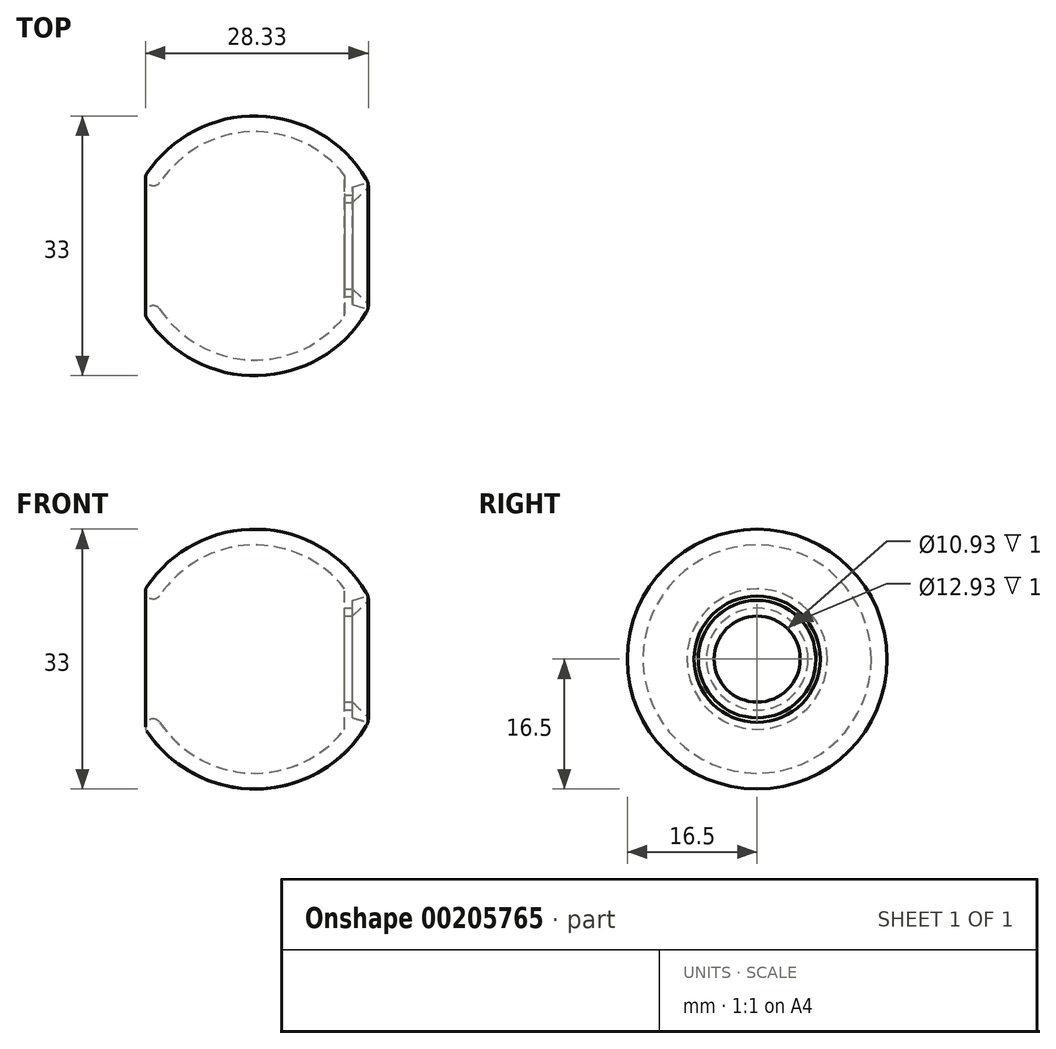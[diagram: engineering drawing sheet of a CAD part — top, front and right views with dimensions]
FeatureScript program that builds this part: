
annotation { "Feature Type Name" : "Feature", "Feature Type Description" : "" }
export const myFeature = defineFeature(function(context is Context, id is Id, definition is map)
    precondition{}
    {
        {
            var Q0;
            Q0=qCreatedBy(makeId("Front.planeOp"),FACE);
            var sketch = newSketch(context, id + "F0", { "sketchPlane" : qUnion([Q0])});
            skArc(sketch, "E0", {"start": v(15.56, 8) * mm, "mid": v(-17.5, 0) * mm, "end": v(15.56, -8) * mm});
            skArc(sketch, "E1", {"start": v(15.56, -8) * mm, "mid": v(19, 0) * mm, "end": v(15.56, 8) * mm});
            skPoint(sketch, "E2", {"position": v(15.56, 8) * mm});
            skPoint(sketch, "E3", {"position": v(15.56, -8) * mm});
            skPoint(sketch, "E4", {"position": v(19, 0) * mm});
            skPoint(sketch, "E5", {"position": v(17.5, 0) * mm});
            skArc(sketch, "E6", {"start": v(15.56, -8) * mm, "mid": v(17.5, 0) * mm, "end": v(15.56, 8) * mm, "construction": true});
            skLineSegment(sketch, "E7", {"start": v(15.56, 8) * mm, "end": v(15.56, -8) * mm, "construction": true});
            skPoint(sketch, "E8", {"position": v(15.56, 0) * mm});
            skSolve(sketch);
        }
        {
            var Q0;
            Q0=qCreatedBy(makeId("Front.planeOp"),FACE);
            var sketch = newSketch(context, id + "F1", { "sketchPlane" : qUnion([Q0])});
            skArc(sketch, "E9.0", {"start": v(14.15, 8.5) * mm, "mid": v(0.4, 16.5) * mm, "end": v(-13.73, 9.15) * mm});
            skLineSegment(sketch, "E10", {"start": v(14.43, 7.46) * mm, "end": v(14.43, 0) * mm, "construction": true});
            skLineSegment(sketch, "E11", {"start": v(14.43, 0) * mm, "end": v(-16.5, 0) * mm, "construction": true});
            skArc(sketch, "E12.0", {"start": v(11.43, 8.92) * mm, "mid": v(-0.54, 14.49) * mm, "end": v(-12.06, 8.05) * mm});
            skPoint(sketch, "E13.orphan", {"position": v(14.43, -8) * mm});
            skLineSegment(sketch, "E14", {"start": v(0, 0) * mm, "end": v(-15.16, 8.75) * mm, "construction": true});
            skLineSegment(sketch, "E15", {"start": v(0, 0) * mm, "end": v(11.25, 13.4) * mm, "construction": true});
            skArc(sketch, "E16", {"start": v(-13.73, 9.15) * mm, "mid": v(-13.45, 7.77) * mm, "end": v(-12.06, 8.05) * mm});
            skPoint(sketch, "E17.visualSharp", {"position": v(14.43, 8) * mm});
            skArc(sketch, "E17.filletArc", {"start": v(14.35, 8.02) * mm, "mid": v(14.27, 8.26) * mm, "end": v(14.15, 8.5) * mm});
            skArc(sketch, "E18", {"start": v(14.43, 7.46) * mm, "mid": v(14.41, 7.74) * mm, "end": v(14.35, 8.02) * mm, "construction": true});
            skLineSegment(sketch, "E19", {"start": v(11.43, 8.92) * mm, "end": v(11.43, 6.46) * mm});
            skLineSegment(sketch, "E20", {"start": v(14.35, 8.02) * mm, "end": v(12.43, 7.46) * mm});
            skLineSegment(sketch, "E21", {"start": v(12.43, 7.46) * mm, "end": v(12.43, 6.46) * mm});
            skLineSegment(sketch, "E22", {"start": v(12.43, 6.46) * mm, "end": v(11.43, 6.46) * mm});
            skSolve(sketch);
        }
        {
            var Q0;
            Q0 = qSketchRegion(id + "F1", true);
            var Q1;
            Q1=sQuery(id+"F1.wireOp",EDGE,"E11");
            revolve(context, id + "F2", {"entities" : qUnion([Q0]), "axis" : qUnion([Q1]), "revolveType" : RevolveType.FULL});
        }
        {
            var Q0;
            Q0=qCreatedBy(makeId("Front.planeOp"),FACE);
            var sketch = newSketch(context, id + "F3", { "sketchPlane" : qUnion([Q0])});
            skArc(sketch, "E23.0", {"start": v(14.43, 7.46) * mm, "mid": v(14.41, 7.74) * mm, "end": v(14.35, 8.02) * mm});
            skLineSegment(sketch, "E23.1", {"start": v(14.35, 8.02) * mm, "end": v(12.43, 7.46) * mm});
            skLineSegment(sketch, "E23.2", {"start": v(12.43, 7.46) * mm, "end": v(12.43, 6.46) * mm});
            skLineSegment(sketch, "E23.3", {"start": v(12.43, 6.46) * mm, "end": v(11.43, 6.46) * mm});
            skLineSegment(sketch, "E24", {"start": v(11.43, 6.46) * mm, "end": v(11.43, 5.46) * mm});
            skLineSegment(sketch, "E25", {"start": v(11.43, 5.46) * mm, "end": v(12.43, 5.46) * mm});
            skLineSegment(sketch, "E26", {"start": v(12.43, 5.46) * mm, "end": v(14.43, 7.46) * mm});
            skLineSegment(sketch, "E27.0", {"start": v(14.43, 0) * mm, "end": v(-16.5, 0) * mm, "construction": true});
            skSolve(sketch);
        }
        {
            var Q0;
            Q0 = qSketchRegion(id + "F3", true);
            var Q1;
            Q1=sQuery(id+"F1.wireOp",EDGE,"E11");
            revolve(context, id + "F4", {"entities" : qUnion([Q0]), "axis" : qUnion([Q1]), "revolveType" : RevolveType.FULL});
        }
    });
